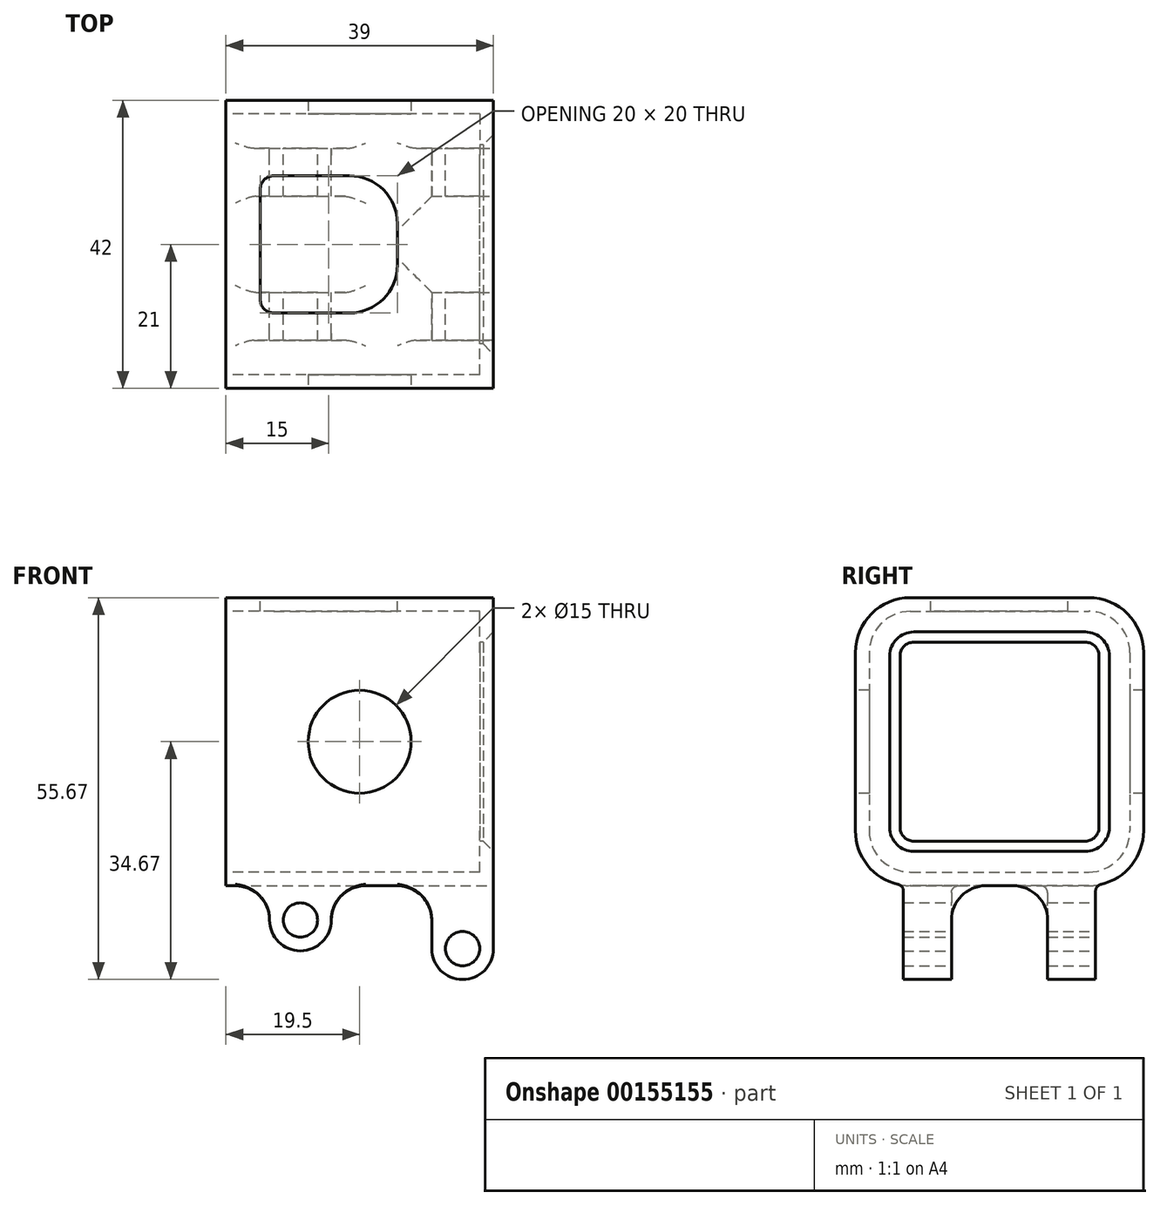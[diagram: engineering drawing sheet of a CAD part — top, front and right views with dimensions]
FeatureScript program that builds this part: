
annotation { "Feature Type Name" : "Feature", "Feature Type Description" : "" }
export const myFeature = defineFeature(function(context is Context, id is Id, definition is map)
    precondition{}
    {
        {
            var Q0;
            Q0=qCreatedBy(makeId("Right.planeOp"),FACE);
            var sketch = newSketch(context, id + "F0", { "sketchPlane" : qUnion([Q0])});
            skLineSegment(sketch, "E0.bottom", {"start": v(-13, 21) * mm, "end": v(13, 21) * mm});
            skLineSegment(sketch, "E0.top", {"start": v(-13, -21) * mm, "end": v(13, -21) * mm});
            skLineSegment(sketch, "E0.left", {"start": v(-21, 13) * mm, "end": v(-21, -13) * mm});
            skLineSegment(sketch, "E0.right", {"start": v(21, 13) * mm, "end": v(21, -13) * mm});
            skLineSegment(sketch, "E1.bottom", {"start": v(-13, 19) * mm, "end": v(13, 19) * mm});
            skLineSegment(sketch, "E1.top", {"start": v(-13, -19) * mm, "end": v(13, -19) * mm});
            skLineSegment(sketch, "E1.left", {"start": v(-19, 13) * mm, "end": v(-19, -13) * mm});
            skLineSegment(sketch, "E1.right", {"start": v(19, 13) * mm, "end": v(19, -13) * mm});
            skPoint(sketch, "E2.visualSharp", {"position": v(-19, 19) * mm});
            skArc(sketch, "E2.filletArc", {"start": v(-13, 19) * mm, "mid": v(-17.24, 17.24) * mm, "end": v(-19, 13) * mm});
            skPoint(sketch, "E3.visualSharp", {"position": v(19, 19) * mm});
            skArc(sketch, "E3.filletArc", {"start": v(19, 13) * mm, "mid": v(17.24, 17.24) * mm, "end": v(13, 19) * mm});
            skPoint(sketch, "E4.visualSharp", {"position": v(19, -19) * mm});
            skArc(sketch, "E4.filletArc", {"start": v(13, -19) * mm, "mid": v(17.24, -17.24) * mm, "end": v(19, -13) * mm});
            skPoint(sketch, "E5.visualSharp", {"position": v(-19, -19) * mm});
            skArc(sketch, "E5.filletArc", {"start": v(-19, -13) * mm, "mid": v(-17.24, -17.24) * mm, "end": v(-13, -19) * mm});
            skPoint(sketch, "E6.visualSharp", {"position": v(-21, -21) * mm});
            skArc(sketch, "E6.filletArc", {"start": v(-21, -13) * mm, "mid": v(-18.66, -18.66) * mm, "end": v(-13, -21) * mm});
            skPoint(sketch, "E7.visualSharp", {"position": v(21, -21) * mm});
            skArc(sketch, "E7.filletArc", {"start": v(13, -21) * mm, "mid": v(18.66, -18.66) * mm, "end": v(21, -13) * mm});
            skPoint(sketch, "E8.visualSharp", {"position": v(21, 21) * mm});
            skArc(sketch, "E8.filletArc", {"start": v(21, 13) * mm, "mid": v(18.66, 18.66) * mm, "end": v(13, 21) * mm});
            skPoint(sketch, "E9.visualSharp", {"position": v(-21, 21) * mm});
            skArc(sketch, "E9.filletArc", {"start": v(-13, 21) * mm, "mid": v(-18.66, 18.66) * mm, "end": v(-21, 13) * mm});
            skSolve(sketch);
        }
        {
            var Q0;
            Q0=qSketchRegion(id+"F0",true);
            extrude(context, id + "F1", {"entities" : qUnion([Q0]), "endBound" : BoundingType.SYMMETRIC, "depth" : 37 * mm});
        }
        {
            var Q0;
            Q0=makeQuery(id+"F1.opExtrude","CAP_FACE",FACE,{"disambiguationData":[OSD([sQuery(id+"F0.wireOp",EDGE,"E0.bottom"),sQuery(id+"F0.wireOp",EDGE,"E0.top"),sQuery(id+"F0.wireOp",EDGE,"E0.left"),sQuery(id+"F0.wireOp",EDGE,"E0.right"),sQuery(id+"F0.wireOp",EDGE,"E1.bottom"),sQuery(id+"F0.wireOp",EDGE,"E1.top"),sQuery(id+"F0.wireOp",EDGE,"E1.left"),sQuery(id+"F0.wireOp",EDGE,"E1.right"),sQuery(id+"F0.wireOp",EDGE,"E2.filletArc"),sQuery(id+"F0.wireOp",EDGE,"E3.filletArc"),sQuery(id+"F0.wireOp",EDGE,"E4.filletArc"),sQuery(id+"F0.wireOp",EDGE,"E5.filletArc"),sQuery(id+"F0.wireOp",EDGE,"E6.filletArc"),sQuery(id+"F0.wireOp",EDGE,"E7.filletArc"),sQuery(id+"F0.wireOp",EDGE,"E8.filletArc"),sQuery(id+"F0.wireOp",EDGE,"E9.filletArc")])],"isStart":false});
            var sketch = newSketch(context, id + "F2", { "sketchPlane" : qUnion([Q0])});
            skLineSegment(sketch, "E10.bottom", {"start": v(-12.5, 14.5) * mm, "end": v(12.5, 14.5) * mm});
            skLineSegment(sketch, "E10.top", {"start": v(-12.5, -14.5) * mm, "end": v(12.5, -14.5) * mm});
            skLineSegment(sketch, "E10.left", {"start": v(-14.5, 12.5) * mm, "end": v(-14.5, -12.5) * mm});
            skLineSegment(sketch, "E10.right", {"start": v(14.5, 12.5) * mm, "end": v(14.5, -12.5) * mm});
            skLineSegment(sketch, "E11.bottom", {"start": v(-13, 21) * mm, "end": v(13, 21) * mm});
            skLineSegment(sketch, "E11.top", {"start": v(-13, -21) * mm, "end": v(13, -21) * mm});
            skLineSegment(sketch, "E11.left", {"start": v(-21, 13) * mm, "end": v(-21, -13) * mm});
            skLineSegment(sketch, "E11.right", {"start": v(21, 13) * mm, "end": v(21, -13) * mm});
            skPoint(sketch, "E12.visualSharp", {"position": v(-21, 21) * mm});
            skArc(sketch, "E12.filletArc", {"start": v(-13, 21) * mm, "mid": v(-18.66, 18.66) * mm, "end": v(-21, 13) * mm});
            skPoint(sketch, "E13.visualSharp", {"position": v(-21, -21) * mm});
            skArc(sketch, "E13.filletArc", {"start": v(-21, -13) * mm, "mid": v(-18.66, -18.66) * mm, "end": v(-13, -21) * mm});
            skPoint(sketch, "E14.visualSharp", {"position": v(21, -21) * mm});
            skArc(sketch, "E14.filletArc", {"start": v(13, -21) * mm, "mid": v(18.66, -18.66) * mm, "end": v(21, -13) * mm});
            skPoint(sketch, "E15.visualSharp", {"position": v(21, 21) * mm});
            skArc(sketch, "E15.filletArc", {"start": v(21, 13) * mm, "mid": v(18.66, 18.66) * mm, "end": v(13, 21) * mm});
            skPoint(sketch, "E16.visualSharp", {"position": v(-14.5, 14.5) * mm});
            skArc(sketch, "E16.filletArc", {"start": v(-12.5, 14.5) * mm, "mid": v(-13.91, 13.91) * mm, "end": v(-14.5, 12.5) * mm});
            skPoint(sketch, "E17.visualSharp", {"position": v(-14.5, -14.5) * mm});
            skArc(sketch, "E17.filletArc", {"start": v(-14.5, -12.5) * mm, "mid": v(-13.91, -13.91) * mm, "end": v(-12.5, -14.5) * mm});
            skPoint(sketch, "E18.visualSharp", {"position": v(14.5, -14.5) * mm});
            skArc(sketch, "E18.filletArc", {"start": v(12.5, -14.5) * mm, "mid": v(13.91, -13.91) * mm, "end": v(14.5, -12.5) * mm});
            skPoint(sketch, "E19.visualSharp", {"position": v(14.5, 14.5) * mm});
            skArc(sketch, "E19.filletArc", {"start": v(14.5, 12.5) * mm, "mid": v(13.91, 13.91) * mm, "end": v(12.5, 14.5) * mm});
            skSolve(sketch);
        }
        {
            var Q0;
            Q0=qSketchRegion(id+"F2",true);
            extrude(context, id + "F3", {"entities" : qUnion([Q0]), "operationType" : NewBodyOperationType.ADD, "depth" : 2 * mm});
        }
        {
            var Q0;
            Q0=makeQuery(id+"F3.opExtrude","CAP_EDGE",EDGE,{"disambiguationData":[OSD([sQuery(id+"F2.wireOp",EDGE,"E10.bottom")])],"isStart":false});
            chamfer(context, id + "F4", {"entities" : qUnion([Q0]), "width" : 1.5 * mm, "tangentPropagation" : true});
        }
        {
            var Q0;
            Q0=makeQuery(id+"F3.boolean.opBoolean","MERGE",FACE,{"derivedFrom":[makeQuery(id+"F1.opExtrude","SWEPT_FACE",FACE,{"disambiguationData":[OSD([sQuery(id+"F0.wireOp",EDGE,"E0.bottom")])]}),makeQuery(id+"F3.opExtrude","SWEPT_FACE",FACE,{"disambiguationData":[OSD([sQuery(id+"F2.wireOp",EDGE,"E11.bottom")])]})]});
            var sketch = newSketch(context, id + "F5", { "sketchPlane" : qUnion([Q0])});
            skLineSegment(sketch, "E20.bottom", {"start": v(-11.5, 10) * mm, "end": v(-0.5, 10) * mm});
            skLineSegment(sketch, "E20.top", {"start": v(-11.5, -10) * mm, "end": v(-0.5, -10) * mm});
            skLineSegment(sketch, "E20.left", {"start": v(-13.5, 8) * mm, "end": v(-13.5, -8) * mm});
            skLineSegment(sketch, "E20.right", {"start": v(6.5, 3) * mm, "end": v(6.5, -3) * mm});
            skPoint(sketch, "E21.visualSharp", {"position": v(-13.5, 10) * mm});
            skArc(sketch, "E21.filletArc", {"start": v(-11.5, 10) * mm, "mid": v(-12.91, 9.41) * mm, "end": v(-13.5, 8) * mm});
            skPoint(sketch, "E22.visualSharp", {"position": v(-13.5, -10) * mm});
            skArc(sketch, "E22.filletArc", {"start": v(-13.5, -8) * mm, "mid": v(-12.91, -9.41) * mm, "end": v(-11.5, -10) * mm});
            skPoint(sketch, "E23.visualSharp", {"position": v(6.5, 10) * mm});
            skArc(sketch, "E23.filletArc", {"start": v(6.5, 3) * mm, "mid": v(4.45, 7.95) * mm, "end": v(-0.5, 10) * mm});
            skPoint(sketch, "E24.visualSharp", {"position": v(6.5, -10) * mm});
            skArc(sketch, "E24.filletArc", {"start": v(-0.5, -10) * mm, "mid": v(4.45, -7.95) * mm, "end": v(6.5, -3) * mm});
            skSolve(sketch);
        }
        {
            var Q0;
            Q0=qSketchRegion(id+"F5",true);
            extrude(context, id + "F6", {"entities" : qUnion([Q0]), "operationType" : NewBodyOperationType.REMOVE, "oppositeDirection" : true, "depth" : 5 * mm});
        }
        {
            var Q0;
            Q0=qCreatedBy(makeId("Front.planeOp"),FACE);
            var sketch = newSketch(context, id + "F7", { "sketchPlane" : qUnion([Q0])});
            skCircle(sketch, "E25", {"center": v(16, -30.17) * mm, "radius": 2.5 * mm});
            skCircle(sketch, "E26", {"center": v(-7.64, -26) * mm, "radius": 2.5 * mm});
            skLineSegment(sketch, "E27", {"start": v(-7.64, -26) * mm, "end": v(16, -30.17) * mm, "construction": true});
            skArc(sketch, "E28", {"start": v(11.5, -30.17) * mm, "mid": v(16, -34.67) * mm, "end": v(20.5, -30.17) * mm});
            skArc(sketch, "E29", {"start": v(-12.14, -26) * mm, "mid": v(-7.64, -30.5) * mm, "end": v(-3.14, -26) * mm});
            skLineSegment(sketch, "E30", {"start": v(20.5, -30.17) * mm, "end": v(20.5, -20) * mm});
            skLineSegment(sketch, "E31", {"start": v(11.5, -30.17) * mm, "end": v(11.5, -20) * mm});
            skLineSegment(sketch, "E32", {"start": v(-3.14, -26) * mm, "end": v(-3.14, -20) * mm});
            skLineSegment(sketch, "E33", {"start": v(-3.14, -20) * mm, "end": v(-12.14, -20) * mm});
            skLineSegment(sketch, "E34", {"start": v(-12.14, -20) * mm, "end": v(-12.14, -26) * mm});
            skLineSegment(sketch, "E35", {"start": v(-3.14, -20) * mm, "end": v(11.5, -20) * mm, "construction": true});
            skLineSegment(sketch, "E36", {"start": v(11.5, -20) * mm, "end": v(20.5, -20) * mm});
            skPoint(sketch, "E36.endSnap0", {"position": v(4.18, -20) * mm});
            skSolve(sketch);
        }
        {
            var Q0;
            Q0=qSketchRegion(id+"F7",true);
            extrude(context, id + "F8", {"entities" : qUnion([Q0]), "operationType" : NewBodyOperationType.ADD, "endBound" : BoundingType.SYMMETRIC, "depth" : 28 * mm});
        }
        {
            var Q0;
            Q0=makeQuery(id+"F8.boolean.opBoolean","INTERSECT",EDGE,{"derivedFrom":[makeQuery(id+"F3.boolean.opBoolean","MERGE",FACE,{"derivedFrom":[makeQuery(id+"F1.opExtrude","SWEPT_FACE",FACE,{"disambiguationData":[OSD([sQuery(id+"F0.wireOp",EDGE,"E0.top")])]}),makeQuery(id+"F3.opExtrude","SWEPT_FACE",FACE,{"disambiguationData":[OSD([sQuery(id+"F2.wireOp",EDGE,"E11.top")])]})]}),makeQuery(id+"F8.opExtrude","SWEPT_FACE",FACE,{"disambiguationData":[OSD([sQuery(id+"F7.wireOp",EDGE,"E34")])]})]});
            var Q1;
            Q1=makeQuery(id+"F8.boolean.opBoolean","INTERSECT",EDGE,{"derivedFrom":[makeQuery(id+"F3.boolean.opBoolean","MERGE",FACE,{"derivedFrom":[makeQuery(id+"F1.opExtrude","SWEPT_FACE",FACE,{"disambiguationData":[OSD([sQuery(id+"F0.wireOp",EDGE,"E0.top")])]}),makeQuery(id+"F3.opExtrude","SWEPT_FACE",FACE,{"disambiguationData":[OSD([sQuery(id+"F2.wireOp",EDGE,"E11.top")])]})]}),makeQuery(id+"F8.opExtrude","SWEPT_FACE",FACE,{"disambiguationData":[OSD([sQuery(id+"F7.wireOp",EDGE,"E32")])]})]});
            var Q2;
            Q2=makeQuery(id+"F8.boolean.opBoolean","INTERSECT",EDGE,{"derivedFrom":[makeQuery(id+"F3.boolean.opBoolean","MERGE",FACE,{"derivedFrom":[makeQuery(id+"F1.opExtrude","SWEPT_FACE",FACE,{"disambiguationData":[OSD([sQuery(id+"F0.wireOp",EDGE,"E0.top")])]}),makeQuery(id+"F3.opExtrude","SWEPT_FACE",FACE,{"disambiguationData":[OSD([sQuery(id+"F2.wireOp",EDGE,"E11.top")])]})]}),makeQuery(id+"F8.opExtrude","SWEPT_FACE",FACE,{"disambiguationData":[OSD([sQuery(id+"F7.wireOp",EDGE,"E31")])]})]});
            fillet(context, id + "F9", {"entities" : qUnion([Q0, Q1, Q2]), "radius" : 5 * mm, "tangentPropagation" : true, "allowEdgeOverflow" : false});
        }
        {
            var Q0;
            Q0=makeQuery(id+"F8.boolean.opBoolean","SPLIT",FACE,{"disambiguationData":[TD([makeQuery(id+"F8.opExtrude","SWEPT_FACE",FACE,{"disambiguationData":[OSD([sQuery(id+"F7.wireOp",EDGE,"E31")])]})])],"derivedFrom":makeQuery(id+"F3.boolean.opBoolean","MERGE",FACE,{"derivedFrom":[makeQuery(id+"F1.opExtrude","SWEPT_FACE",FACE,{"disambiguationData":[OSD([sQuery(id+"F0.wireOp",EDGE,"E0.top")])]}),makeQuery(id+"F3.opExtrude","SWEPT_FACE",FACE,{"disambiguationData":[OSD([sQuery(id+"F2.wireOp",EDGE,"E11.top")])]})]})});
            var sketch = newSketch(context, id + "F10", { "sketchPlane" : qUnion([Q0])});
            skLineSegment(sketch, "E37.bottom", {"start": v(-18.5, 7) * mm, "end": v(20.5, 7) * mm});
            skLineSegment(sketch, "E37.top", {"start": v(-18.5, -7) * mm, "end": v(20.5, -7) * mm});
            skLineSegment(sketch, "E37.left", {"start": v(-18.5, 7) * mm, "end": v(-18.5, -7) * mm});
            skLineSegment(sketch, "E37.right", {"start": v(20.5, 7) * mm, "end": v(20.5, -7) * mm});
            skSolve(sketch);
        }
        {
            var Q0;
            Q0 = qSketchRegion(id + "F10", true);
            extrude(context, id + "F11", {"entities" : qUnion([Q0]), "operationType" : NewBodyOperationType.REMOVE, "depth" : 25 * mm});
        }
        {
            var Q0;
            {var subQ2=sQuery(id+"F10.wireOp",EDGE,"E37.bottom");Q0=makeQuery(id+"F11.boolean.opBoolean","COPY",EDGE,{"disambiguationData":[TD([makeQuery(id+"F8.opExtrude","SWEPT_FACE",FACE,{"disambiguationData":[OSD([sQuery(id+"F7.wireOp",EDGE,"E30")])]})])],"derivedFrom":makeQuery(id+"F11.opExtrude","CAP_EDGE",EDGE,{"disambiguationData":[OSD([subQ2])],"isStart":true})});}
            var Q1;
            {var subQ2=sQuery(id+"F10.wireOp",EDGE,"E37.top");Q1=makeQuery(id+"F11.boolean.opBoolean","COPY",EDGE,{"disambiguationData":[TD([makeQuery(id+"F8.opExtrude","SWEPT_FACE",FACE,{"disambiguationData":[OSD([sQuery(id+"F7.wireOp",EDGE,"E30")])]})])],"derivedFrom":makeQuery(id+"F11.opExtrude","CAP_EDGE",EDGE,{"disambiguationData":[OSD([subQ2])],"isStart":true})});}
            fillet(context, id + "F12", {"entities" : qUnion([Q0, Q1]), "radius" : 5 * mm, "tangentPropagation" : true, "allowEdgeOverflow" : false});
        }
        {
            var Q0;
            Q0=makeQuery(id+"F8.boolean.opBoolean","INTERSECT",EDGE,{"derivedFrom":[makeQuery(id+"F3.boolean.opBoolean","MERGE",FACE,{"derivedFrom":[makeQuery(id+"F1.opExtrude","SWEPT_FACE",FACE,{"disambiguationData":[OSD([sQuery(id+"F0.wireOp",EDGE,"E6.filletArc")])]}),makeQuery(id+"F3.opExtrude","SWEPT_FACE",FACE,{"disambiguationData":[OSD([sQuery(id+"F2.wireOp",EDGE,"E13.filletArc")])]})]}),makeQuery(id+"F8.opExtrude","CAP_FACE",FACE,{"disambiguationData":[OSD([sQuery(id+"F7.wireOp",EDGE,"E25"),sQuery(id+"F7.wireOp",EDGE,"E28"),sQuery(id+"F7.wireOp",EDGE,"E30"),sQuery(id+"F7.wireOp",EDGE,"E31"),sQuery(id+"F7.wireOp",EDGE,"E36")])],"isStart":false})]});
            var Q1;
            Q1=makeQuery(id+"F8.boolean.opBoolean","INTERSECT",EDGE,{"derivedFrom":[makeQuery(id+"F3.boolean.opBoolean","MERGE",FACE,{"derivedFrom":[makeQuery(id+"F1.opExtrude","SWEPT_FACE",FACE,{"disambiguationData":[OSD([sQuery(id+"F0.wireOp",EDGE,"E6.filletArc")])]}),makeQuery(id+"F3.opExtrude","SWEPT_FACE",FACE,{"disambiguationData":[OSD([sQuery(id+"F2.wireOp",EDGE,"E13.filletArc")])]})]}),makeQuery(id+"F8.opExtrude","CAP_FACE",FACE,{"disambiguationData":[OSD([sQuery(id+"F7.wireOp",EDGE,"E26"),sQuery(id+"F7.wireOp",EDGE,"E29"),sQuery(id+"F7.wireOp",EDGE,"E32"),sQuery(id+"F7.wireOp",EDGE,"E33"),sQuery(id+"F7.wireOp",EDGE,"E34")])],"isStart":false})]});
            var Q2;
            Q2=makeQuery(id+"F8.boolean.opBoolean","INTERSECT",EDGE,{"derivedFrom":[makeQuery(id+"F3.boolean.opBoolean","MERGE",FACE,{"derivedFrom":[makeQuery(id+"F1.opExtrude","SWEPT_FACE",FACE,{"disambiguationData":[OSD([sQuery(id+"F0.wireOp",EDGE,"E7.filletArc")])]}),makeQuery(id+"F3.opExtrude","SWEPT_FACE",FACE,{"disambiguationData":[OSD([sQuery(id+"F2.wireOp",EDGE,"E14.filletArc")])]})]}),makeQuery(id+"F8.opExtrude","CAP_FACE",FACE,{"disambiguationData":[OSD([sQuery(id+"F7.wireOp",EDGE,"E25"),sQuery(id+"F7.wireOp",EDGE,"E28"),sQuery(id+"F7.wireOp",EDGE,"E30"),sQuery(id+"F7.wireOp",EDGE,"E31"),sQuery(id+"F7.wireOp",EDGE,"E36")])],"isStart":true})]});
            var Q3;
            Q3=makeQuery(id+"F8.boolean.opBoolean","INTERSECT",EDGE,{"derivedFrom":[makeQuery(id+"F3.boolean.opBoolean","MERGE",FACE,{"derivedFrom":[makeQuery(id+"F1.opExtrude","SWEPT_FACE",FACE,{"disambiguationData":[OSD([sQuery(id+"F0.wireOp",EDGE,"E7.filletArc")])]}),makeQuery(id+"F3.opExtrude","SWEPT_FACE",FACE,{"disambiguationData":[OSD([sQuery(id+"F2.wireOp",EDGE,"E14.filletArc")])]})]}),makeQuery(id+"F8.opExtrude","CAP_FACE",FACE,{"disambiguationData":[OSD([sQuery(id+"F7.wireOp",EDGE,"E26"),sQuery(id+"F7.wireOp",EDGE,"E29"),sQuery(id+"F7.wireOp",EDGE,"E32"),sQuery(id+"F7.wireOp",EDGE,"E33"),sQuery(id+"F7.wireOp",EDGE,"E34")])],"isStart":true})]});
            var Q4;
            {var subQ0=sQuery(id+"F2.wireOp",EDGE,"E11.top");var subQ1=sQuery(id+"F0.wireOp",EDGE,"E0.top");var subQ2=sQuery(id+"F10.wireOp",EDGE,"E37.top");Q4=makeQuery(id+"F11.boolean.opBoolean","COPY",EDGE,{"disambiguationData":[TD([makeQuery(id+"F9.opFillet","BLEND_FACE",FACE,{"disambiguationData":[OSD([subQ1,subQ0,sQuery(id+"F7.wireOp",EDGE,"E32")])]})])],"derivedFrom":makeQuery(id+"F11.opExtrude","CAP_EDGE",EDGE,{"disambiguationData":[OSD([subQ2])],"isStart":true})});}
            var Q5;
            {var subQ0=sQuery(id+"F2.wireOp",EDGE,"E11.top");var subQ1=sQuery(id+"F0.wireOp",EDGE,"E0.top");var subQ2=sQuery(id+"F10.wireOp",EDGE,"E37.bottom");Q5=makeQuery(id+"F11.boolean.opBoolean","COPY",EDGE,{"disambiguationData":[TD([makeQuery(id+"F9.opFillet","BLEND_FACE",FACE,{"disambiguationData":[OSD([subQ1,subQ0,sQuery(id+"F7.wireOp",EDGE,"E32")])]})])],"derivedFrom":makeQuery(id+"F11.opExtrude","CAP_EDGE",EDGE,{"disambiguationData":[OSD([subQ2])],"isStart":true})});}
            fillet(context, id + "F13", {"entities" : qUnion([Q0, Q1, Q2, Q3, Q4, Q5]), "radius" : 1 * mm, "tangentPropagation" : true, "allowEdgeOverflow" : false});
        }
        {
            var Q0;
            Q0=qCreatedBy(makeId("Front.planeOp"),FACE);
            var sketch = newSketch(context, id + "F14", { "sketchPlane" : qUnion([Q0])});
            skCircle(sketch, "E38", {"center": v(1, 0) * mm, "radius": 7.5 * mm});
            skSolve(sketch);
        }
        {
            var Q0;
            Q0 = qSketchRegion(id + "F14", true);
            extrude(context, id + "F15", {"entities" : qUnion([Q0]), "operationType" : NewBodyOperationType.REMOVE, "endBound" : BoundingType.SYMMETRIC, "oppositeDirection" : true, "depth" : 45 * mm});
        }
    });
